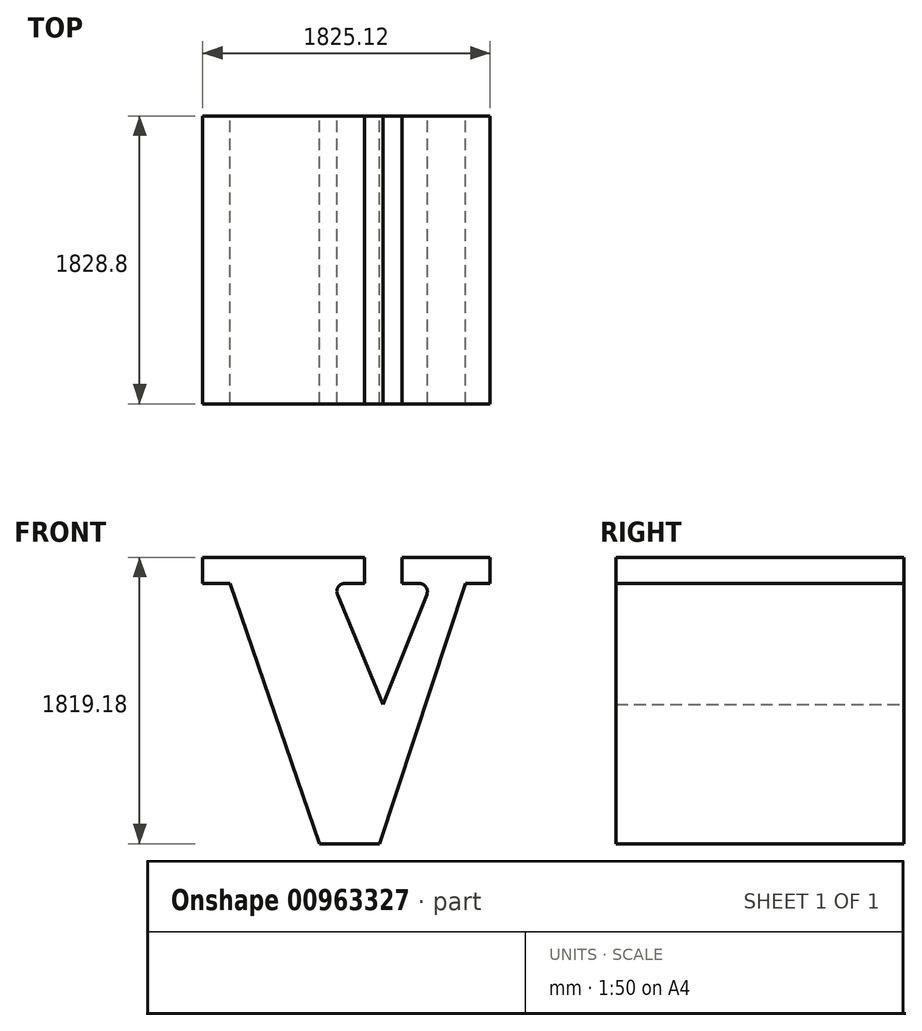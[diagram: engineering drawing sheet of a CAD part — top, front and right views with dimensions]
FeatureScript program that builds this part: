
annotation { "Feature Type Name" : "Feature", "Feature Type Description" : "" }
export const myFeature = defineFeature(function(context is Context, id is Id, definition is map)
    precondition{}
    {
        {
            var Q0;
            Q0=qCreatedBy(makeId("Front.planeOp"),FACE);
            var sketch = newSketch(context, id + "F0", { "sketchPlane" : qUnion([Q0])});
            skLineSegment(sketch, "E0", {"start": v(-931.03, 756.06) * mm, "end": v(-758.63, 756.06) * mm});
            skLineSegment(sketch, "E1", {"start": v(-758.63, 756.06) * mm, "end": v(-187.9, -896.66) * mm});
            skLineSegment(sketch, "E2", {"start": v(-187.9, -896.66) * mm, "end": v(192.57, -896.66) * mm});
            skLineSegment(sketch, "E3", {"start": v(192.57, -896.66) * mm, "end": v(739.52, 756.06) * mm});
            skLineSegment(sketch, "E4", {"start": v(739.52, 756.06) * mm, "end": v(894.09, 756.06) * mm});
            skLineSegment(sketch, "E5", {"start": v(894.09, 756.06) * mm, "end": v(894.09, 922.52) * mm});
            skLineSegment(sketch, "E6", {"start": v(-75.53, 685.89) * mm, "end": v(215.78, -11.71) * mm});
            skLineSegment(sketch, "E7", {"start": v(492.06, 686.57) * mm, "end": v(215.78, -11.71) * mm});
            skLineSegment(sketch, "E8", {"start": v(444.82, 756.06) * mm, "end": v(335.25, 756.06) * mm});
            skLineSegment(sketch, "E9", {"start": v(335.25, 756.06) * mm, "end": v(335.25, 922.52) * mm});
            skLineSegment(sketch, "E10", {"start": v(-28.65, 756.26) * mm, "end": v(97.45, 756.26) * mm});
            skLineSegment(sketch, "E11", {"start": v(97.45, 756.26) * mm, "end": v(97.45, 922.52) * mm});
            skLineSegment(sketch, "E12", {"start": v(97.45, 922.52) * mm, "end": v(-931.03, 922.52) * mm});
            skLineSegment(sketch, "E13", {"start": v(335.25, 922.52) * mm, "end": v(894.09, 922.52) * mm});
            skPoint(sketch, "E14.visualSharp", {"position": v(-104.92, 756.26) * mm});
            skLineSegment(sketch, "E15", {"start": v(-931.03, 922.52) * mm, "end": v(-931.03, 756.06) * mm});
            skPoint(sketch, "E16.visualSharp", {"position": v(519.55, 756.06) * mm});
            skArc(sketch, "E16.filletArc", {"start": v(492.06, 686.57) * mm, "mid": v(486.83, 733.81) * mm, "end": v(444.82, 756.06) * mm});
            skArc(sketch, "E17.filletArc", {"start": v(-28.65, 756.26) * mm, "mid": v(-70.93, 733.62) * mm, "end": v(-75.53, 685.89) * mm});
            skSolve(sketch);
        }
        {
            var Q0;
            Q0 = qSketchRegion(id + "F0", true);
            extrude(context, id + "F1", {"entities" : qUnion([Q0]), "depth" : 1828.8 * mm, "offsetDistance" : 25 * mm});
        }
    });
